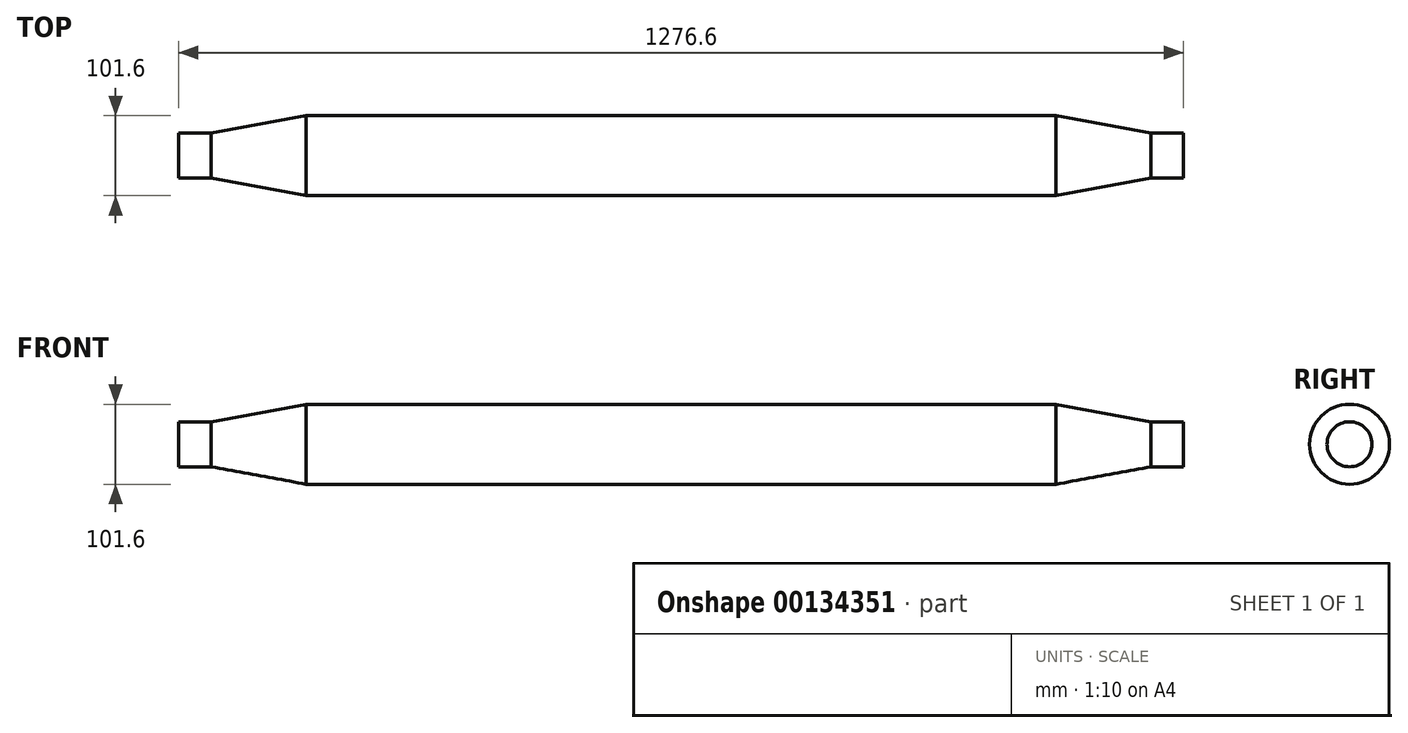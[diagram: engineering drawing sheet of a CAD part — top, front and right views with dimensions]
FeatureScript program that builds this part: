
annotation { "Feature Type Name" : "Feature", "Feature Type Description" : "" }
export const myFeature = defineFeature(function(context is Context, id is Id, definition is map)
    precondition{}
    {
        {
            var Q0;
            Q0=qCreatedBy(makeId("Right.planeOp"),FACE);
            var sketch = newSketch(context, id + "F0", { "sketchPlane" : qUnion([Q0])});
            skCircle(sketch, "E0", {"center": v(0, 0) * mm, "radius": 50.8 * mm});
            skSolve(sketch);
        }
        {
            var Q0;
            Q0=qSketchRegion(id+"F0",true);
            extrude(context, id + "F1", {"entities" : qUnion([Q0]), "endBound" : BoundingType.SYMMETRIC, "depth" : 952.5 * mm});
        }
        {
            var Q0;
            Q0=qCreatedBy(makeId("Right.planeOp"),FACE);
            cPlane(context, id + "F2", {"entities" : qUnion([Q0]), "cplaneType" : CPlaneType.OFFSET, "offset" : 638.3 * mm, "width" : 152.4 * mm, "height" : 152.4 * mm});
        }
        {
            var Q0;
            Q0=qCreatedBy(id+"F2.planeOp",FACE);
            var sketch = newSketch(context, id + "F3", { "sketchPlane" : qUnion([Q0])});
            skCircle(sketch, "E1", {"center": v(0, 0) * mm, "radius": 28.58 * mm});
            skSolve(sketch);
        }
        {
            var Q0;
            Q0=qSketchRegion(id+"F3",true);
            extrude(context, id + "F4", {"entities" : qUnion([Q0]), "oppositeDirection" : true, "depth" : 41.4 * mm});
        }
        {
            var Q0;
            Q0=makeQuery(id+"F4.opExtrude","SWEPT_BODY",BODY,{"disambiguationData":[OSD([sQuery(id+"F3.wireOp",EDGE,"E1")])]});
            var Q1;
            Q1=qCreatedBy(makeId("Right.planeOp"),FACE);
            mirror(context, id + "F5", {"entities" : qUnion([Q0]), "mirrorPlane" : qUnion([Q1])});
        }
        {
            var Q0;
            Q0=makeQuery(id+"F1.opExtrude","CAP_FACE",FACE,{"disambiguationData":[OSD([sQuery(id+"F0.wireOp",EDGE,"E0")])],"isStart":false});
            var Q1;
            Q1=makeQuery(id+"F4.opExtrude","CAP_FACE",FACE,{"disambiguationData":[OSD([sQuery(id+"F3.wireOp",EDGE,"E1")])],"isStart":false});
            loft(context, id + "F6", {"sheetProfilesArray" : [{ "sheetProfileEntities" : qUnion([Q0]) }, { "sheetProfileEntities" : qUnion([Q1]) }]});
        }
        {
            var Q0;
            Q0=makeQuery(id+"F1.opExtrude","CAP_FACE",FACE,{"disambiguationData":[OSD([sQuery(id+"F0.wireOp",EDGE,"E0")])],"isStart":true});
            var Q1;
            Q1=makeQuery(id+"F5.opPattern","COPY",FACE,{"derivedFrom":makeQuery(id+"F4.opExtrude","CAP_FACE",FACE,{"disambiguationData":[OSD([sQuery(id+"F3.wireOp",EDGE,"E1")])],"isStart":false}),"instanceName":"1"});
            loft(context, id + "F7", {"sheetProfilesArray" : [{ "sheetProfileEntities" : qUnion([Q0]) }, { "sheetProfileEntities" : qUnion([Q1]) }]});
        }
    });
